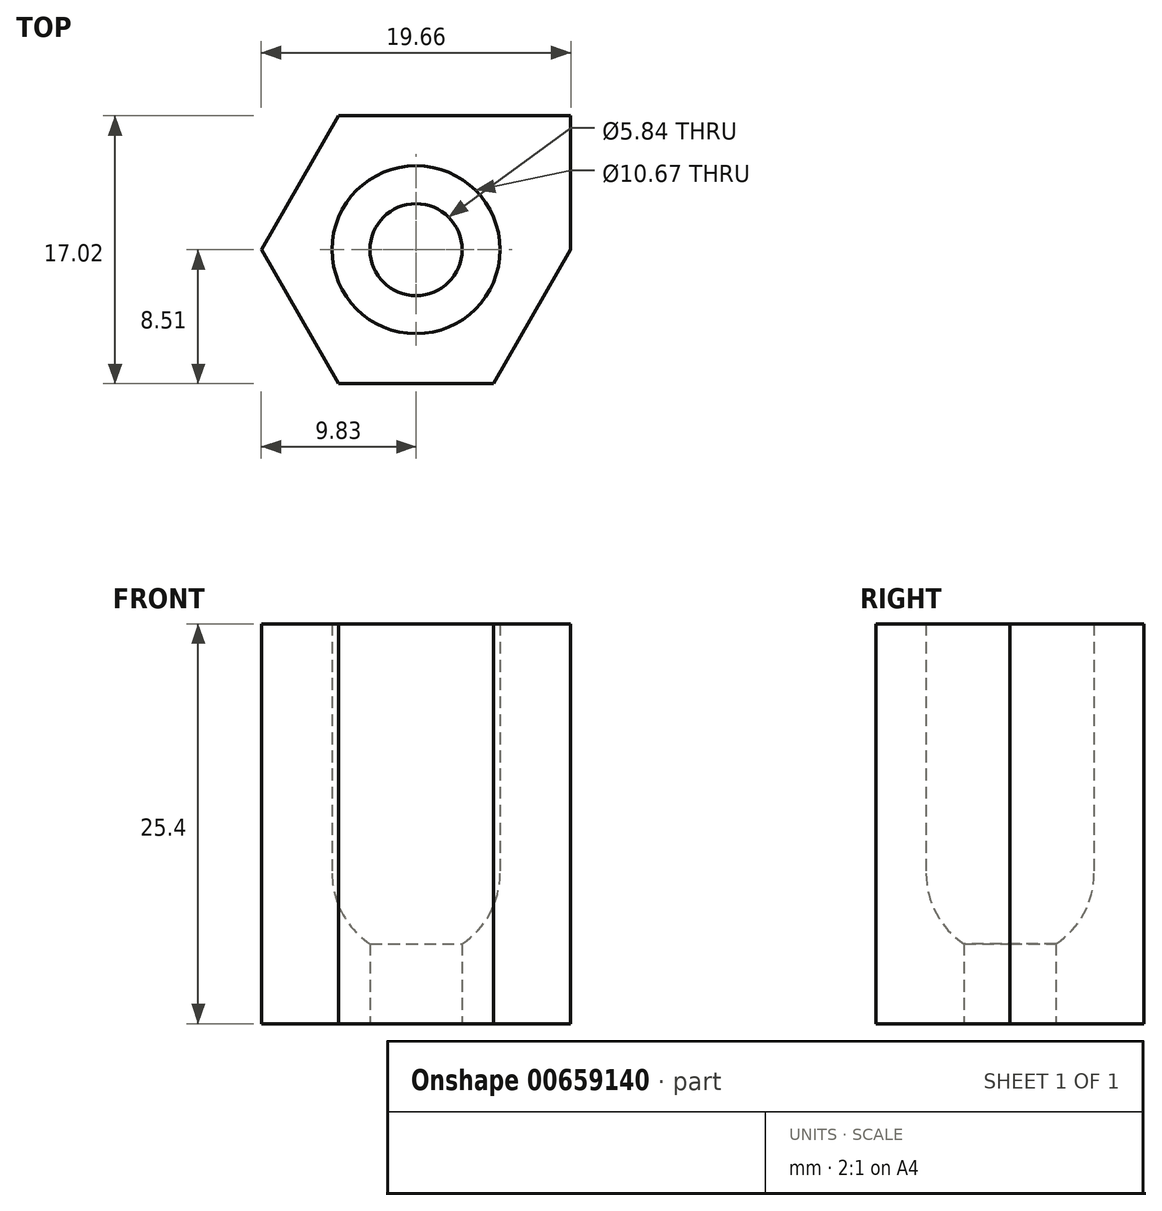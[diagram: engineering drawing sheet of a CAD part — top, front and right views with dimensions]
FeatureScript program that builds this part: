
annotation { "Feature Type Name" : "Feature", "Feature Type Description" : "" }
export const myFeature = defineFeature(function(context is Context, id is Id, definition is map)
    precondition{}
    {
        {
            var Q0;
            Q0=qCreatedBy(makeId("Top.planeOp"),FACE);
            var sketch = newSketch(context, id + "F0", { "sketchPlane" : qUnion([Q0])});
            skCircle(sketch, "E0", {"center": v(0, 0) * mm, "radius": 5.33 * mm});
            skCircle(sketch, "E1.cCircle", {"center": v(0, 0) * mm, "radius": 8.5 * mm, "construction": true});
            skLineSegment(sketch, "E1.0", {"start": v(-4.91, 8.5) * mm, "end": v(4.91, 8.5) * mm});
            skLineSegment(sketch, "E1.1", {"start": v(4.91, 8.5) * mm, "end": v(9.83, 0) * mm});
            skLineSegment(sketch, "E1.2", {"start": v(9.83, 0) * mm, "end": v(4.91, -8.5) * mm});
            skLineSegment(sketch, "E1.3", {"start": v(4.91, -8.5) * mm, "end": v(-4.91, -8.5) * mm});
            skLineSegment(sketch, "E1.4", {"start": v(-4.91, -8.5) * mm, "end": v(-9.83, 0) * mm});
            skLineSegment(sketch, "E1.5", {"start": v(-9.83, 0) * mm, "end": v(-4.91, 8.5) * mm});
            skPoint(sketch, "E1.0.midPoint", {"position": v(0, 8.5) * mm});
            skLineSegment(sketch, "E2", {"start": v(4.91, 8.5) * mm, "end": v(9.83, 8.5) * mm});
            skLineSegment(sketch, "E3", {"start": v(9.83, 8.5) * mm, "end": v(9.83, 0) * mm});
            skSolve(sketch);
        }
        {
            var Q0;
            Q0 = qSketchRegion(id + "F0", true);
            var Q1;
            Q1=makeQuery(id+"F0.imprint","IMPRINT",FACE,{"disambiguationData":[TD([[makeQuery(id+"F0.imprint","IMPRINT",EDGE,{"derivedFrom":sQuery(id+"F0.wireOp",EDGE,"E0")}),1.0]])]});
            extrude(context, id + "F1", {"entities" : qUnion([Q0, Q1]), "depth" : 25.4 * mm, "offsetDistance" : 25.4 * mm});
        }
        {
            var Q0;
            Q0=qCreatedBy(makeId("Front.planeOp"),FACE);
            var sketch = newSketch(context, id + "F2", { "sketchPlane" : qUnion([Q0])});
            skLineSegment(sketch, "E4", {"start": v(-2.92, 0) * mm, "end": v(-2.92, 5.08) * mm});
            skLineSegment(sketch, "E5", {"start": v(-2.92, 0) * mm, "end": v(0, 0) * mm});
            skArc(sketch, "E6", {"start": v(-2.92, 5.08) * mm, "mid": v(-4.7, 7) * mm, "end": v(-5.33, 9.54) * mm});
            skLineSegment(sketch, "E7", {"start": v(-5.33, 9.54) * mm, "end": v(-5.33, 28.88) * mm});
            skLineSegment(sketch, "E8", {"start": v(-5.33, 28.88) * mm, "end": v(0, 28.88) * mm});
            skLineSegment(sketch, "E9", {"start": v(0, 28.88) * mm, "end": v(0, 0) * mm});
            skLineSegment(sketch, "E10", {"start": v(0, 28.88) * mm, "end": v(0, 0) * mm, "construction": true});
            skSolve(sketch);
        }
        {
            var Q0;
            Q0 = qSketchRegion(id + "F2", true);
            var Q1;
            Q1=sQuery(id+"F2.wireOp",EDGE,"E9");
            revolve(context, id + "F3", {"operationType" : NewBodyOperationType.REMOVE, "entities" : qUnion([Q0]), "axis" : qUnion([Q1]), "revolveType" : RevolveType.FULL, "oppositeDirection" : true});
        }
    });
